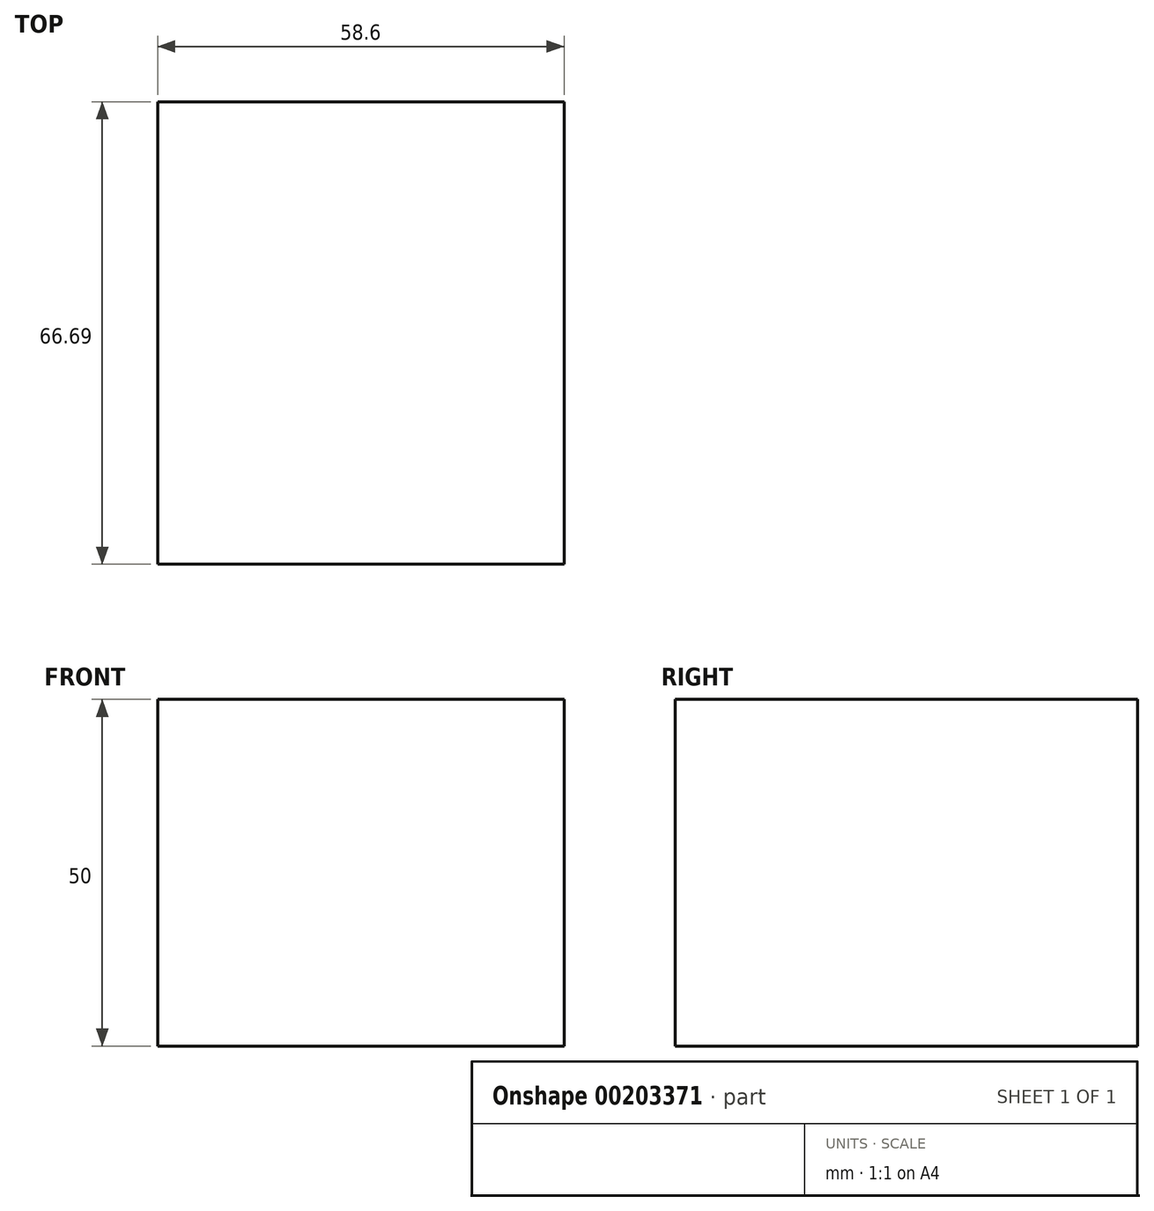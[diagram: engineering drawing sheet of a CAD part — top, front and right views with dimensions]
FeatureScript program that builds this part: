
annotation { "Feature Type Name" : "Feature", "Feature Type Description" : "" }
export const myFeature = defineFeature(function(context is Context, id is Id, definition is map)
    precondition{}
    {
        {
            var Q0;
            Q0=qCreatedBy(makeId("Top.planeOp"),FACE);
            var sketch = newSketch(context, id + "F0", { "sketchPlane" : qUnion([Q0])});
            skLineSegment(sketch, "E0.bottom", {"start": v(0, 0) * mm, "end": v(58.6, 0) * mm});
            skLineSegment(sketch, "E0.top", {"start": v(0, 66.69) * mm, "end": v(58.6, 66.69) * mm});
            skLineSegment(sketch, "E0.left", {"start": v(0, 0) * mm, "end": v(0, 66.69) * mm});
            skLineSegment(sketch, "E0.right", {"start": v(58.6, 0) * mm, "end": v(58.6, 66.69) * mm});
            skSolve(sketch);
        }
        {
            var Q0;
            Q0=makeQuery(id+"F0.imprint","IMPRINT",FACE,{"disambiguationData":[TD([[makeQuery(id+"F0.imprint","IMPRINT",EDGE,{"derivedFrom":sQuery(id+"F0.wireOp",EDGE,"E0.bottom")}),1.0]])]});
            extrude(context, id + "F1", {"entities" : qUnion([Q0]), "depth" : 50 * mm});
        }
    });
